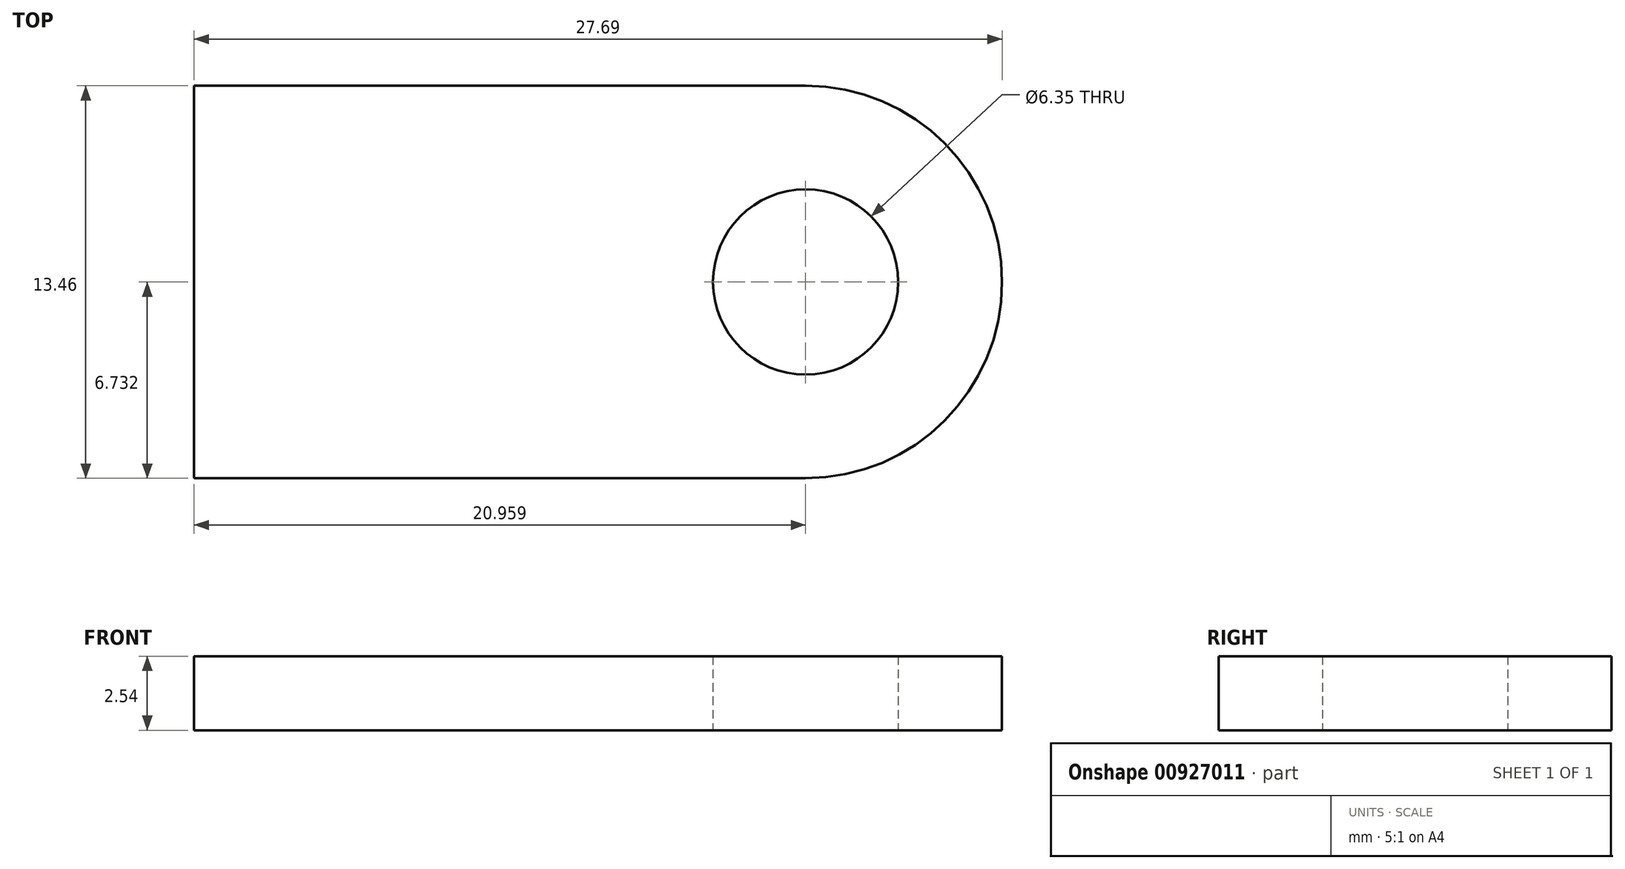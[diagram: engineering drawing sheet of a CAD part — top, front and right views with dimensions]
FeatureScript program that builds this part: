
annotation { "Feature Type Name" : "Feature", "Feature Type Description" : "" }
export const myFeature = defineFeature(function(context is Context, id is Id, definition is map)
    precondition{}
    {
        {
            var Q0;
            Q0=qCreatedBy(makeId("Top.planeOp"),FACE);
            var sketch = newSketch(context, id + "F0", { "sketchPlane" : qUnion([Q0])});
            skLineSegment(sketch, "E0.bottom", {"start": v(-16.82, -6.09) * mm, "end": v(4.14, -6.09) * mm});
            skLineSegment(sketch, "E0.top", {"start": v(-16.82, -19.55) * mm, "end": v(4.14, -19.55) * mm});
            skLineSegment(sketch, "E0.left", {"start": v(-16.82, -6.09) * mm, "end": v(-16.82, -19.55) * mm});
            skLineSegment(sketch, "E0.right", {"start": v(10.87, -12.82) * mm, "end": v(10.87, -12.82) * mm});
            skPoint(sketch, "E1.visualSharp", {"position": v(10.87, -6.09) * mm});
            skArc(sketch, "E1.filletArc", {"start": v(10.87, -12.82) * mm, "mid": v(8.9, -8.06) * mm, "end": v(4.14, -6.09) * mm});
            skPoint(sketch, "E2.visualSharp", {"position": v(10.87, -19.55) * mm});
            skArc(sketch, "E2.filletArc", {"start": v(4.14, -19.55) * mm, "mid": v(8.9, -17.58) * mm, "end": v(10.87, -12.82) * mm});
            skCircle(sketch, "E3", {"center": v(4.14, -12.82) * mm, "radius": 3.18 * mm});
            skSolve(sketch);
        }
        {
            var Q0;
            Q0 = qSketchRegion(id + "F0", true);
            extrude(context, id + "F1", {"entities" : qUnion([Q0]), "depth" : 2.54 * mm, "offsetDistance" : 25.4 * mm});
        }
    });
